# Revit family: CANOE LED PENDANT LIGHT
name_source: partatom
category: Lighting Fixtures
units: mm (PartAtom-declared; Revit-internal decimal feet)

## family parameters
Cut with Voids When Loaded = No
Host = Face
Light Source = Yes
Part Type = Normal
Room Calculation Point = No
Round Connector Dimension = Use Diameter
Shared = No

## types (4) — shared parameters
Apparent Load = 0 VA
Average life based on 77F(HRS) = 50000
CRI = >80
Color Filter = 16777215
Default Elevation = 0' - 0"
Description = The Canoe pendant body is constructed of high quality, die-cast aluminum alloy, and features a recessed honeycomb lens
Dimming / Control = 1-10 V
Dimming Lamp Color Temperature Shift = <None>
Fixture Height = 4' - 0"
Fixture Length = 4' - 7 1/8"
IP Rating = 20
Load Classification = Lighting
Manufacturer = Above All Lighting
Power Factor = 1
Suspender Material = Aluminum
Tilt Angle = -90.00°
Type Comments = CANOE LED PENDANT LIGHT
URL = https://www.abovealllighting.com
Voltage = 120-347 V
Wattage Comments = 35 W

## per-type parameters (varying)
| type | Finish/Color | Model | Order number | Photometric Web File |
| CANO35-40808 | Aluminum White | CANO28-40808 | 16224 | CANO35-40808.IES |
| CANO28-40808-OR | Orange | CANO28-40808-OR | 16227 | CANO28-40808.IES |
| CANO28-40808-BU | ALUMINUM _BLUE | CANO28-40808-BU | 16226 | CANO28-40808.IES |
| CANO28-40808-GY | Grey | CANO28-40808-GY | 16225 | CANO28-40808.IES |

## geometry (parser evidence)
native form markers: Sweep x6
no freeform markers — native parametric forms only
